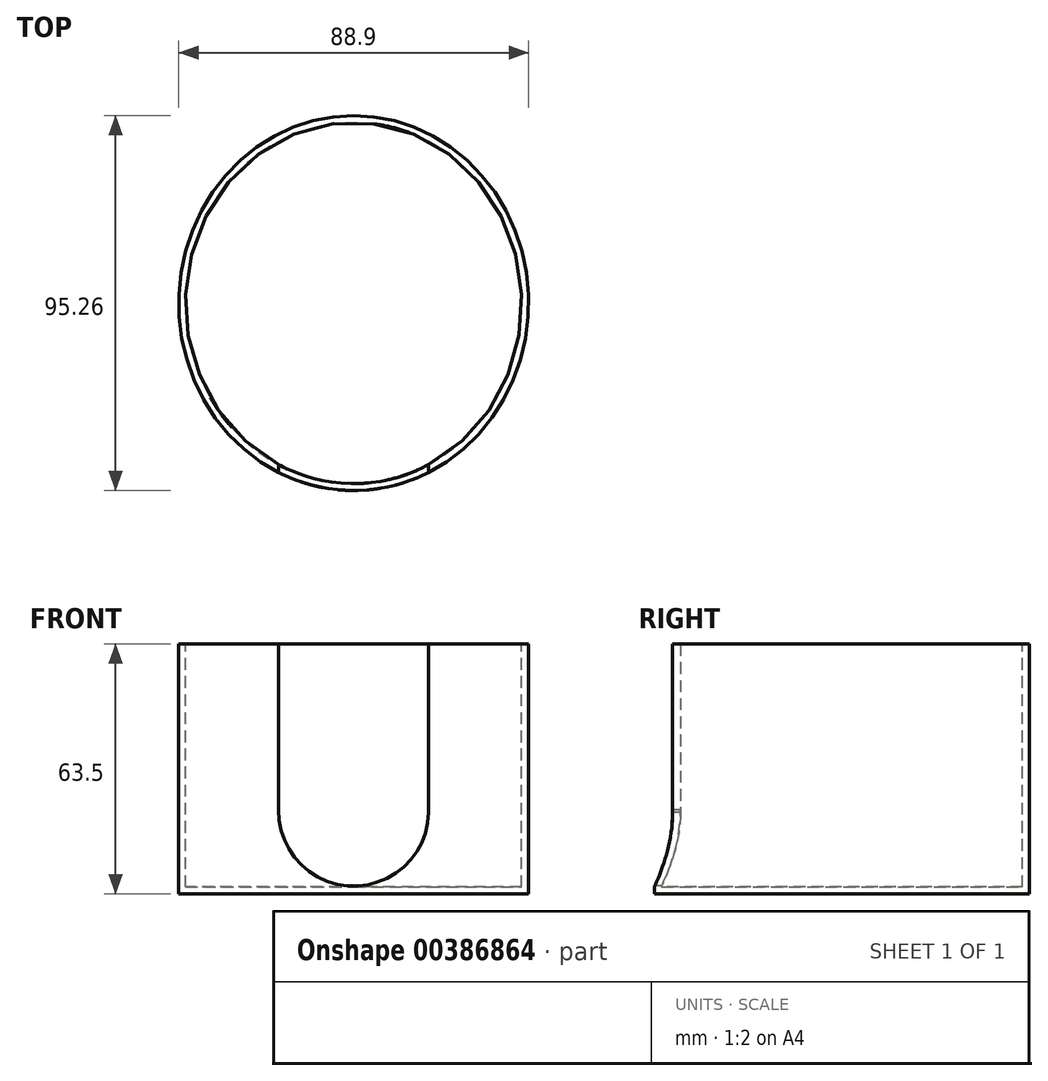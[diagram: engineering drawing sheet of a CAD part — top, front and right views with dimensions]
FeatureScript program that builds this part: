
annotation { "Feature Type Name" : "Feature", "Feature Type Description" : "" }
export const myFeature = defineFeature(function(context is Context, id is Id, definition is map)
    precondition{}
    {
        {
            var Q0;
            Q0=qCreatedBy(makeId("Top.planeOp"),FACE);
            var sketch = newSketch(context, id + "F0", { "sketchPlane" : qUnion([Q0])});
            skEllipse(sketch, "E0", {"center": v(0, 0) * mm, "majorRadius": 47.63 * mm, "minorRadius": 44.45 * mm, "majorAxis": v(0, 1)});
            skSolve(sketch);
        }
        {
            var Q0;
            Q0=makeQuery(id+"F0.imprint","IMPRINT",FACE,{"disambiguationData":[TD([[makeQuery(id+"F0.imprint","IMPRINT",EDGE,{"derivedFrom":sQuery(id+"F0.wireOp",EDGE,"E0")}),1.0]])]});
            extrude(context, id + "F1", {"entities" : qUnion([Q0]), "depth" : 63.5 * mm});
        }
        {
            var Q0;
            Q0=makeQuery(id+"F1.opExtrude","CAP_FACE",FACE,{"disambiguationData":[OSD([sQuery(id+"F0.wireOp",EDGE,"E0")])],"isStart":false});
            shell(context, id + "F2", {"entities" : qUnion([Q0]), "thickness" : 1.75 * mm});
        }
        {
            var Q0;
            Q0=qCreatedBy(makeId("Front.planeOp"),FACE);
            cPlane(context, id + "F3", {"entities" : qUnion([Q0]), "cplaneType" : CPlaneType.OFFSET, "offset" : 47.62 * mm, "width" : 152.4 * mm, "height" : 152.4 * mm});
        }
        {
            var Q0;
            Q0=qCreatedBy(id+"F3.planeOp",FACE);
            var sketch = newSketch(context, id + "F4", { "sketchPlane" : qUnion([Q0])});
            skCircle(sketch, "E1", {"center": v(0, 21.05) * mm, "radius": 19.05 * mm});
            skLineSegment(sketch, "E2.bottom", {"start": v(-19.05, 20.7) * mm, "end": v(19.05, 20.7) * mm});
            skLineSegment(sketch, "E2.top", {"start": v(-19.05, 63.88) * mm, "end": v(19.05, 63.88) * mm});
            skLineSegment(sketch, "E2.left", {"start": v(-19.05, 20.7) * mm, "end": v(-19.05, 63.88) * mm});
            skLineSegment(sketch, "E2.right", {"start": v(19.05, 20.7) * mm, "end": v(19.05, 63.88) * mm});
            skSolve(sketch);
        }
        {
            var Q0;
            Q0 = qSketchRegion(id + "F4", true);
            extrude(context, id + "F5", {"entities" : qUnion([Q0]), "operationType" : NewBodyOperationType.REMOVE, "oppositeDirection" : true, "depth" : 8 * mm});
        }
    });
